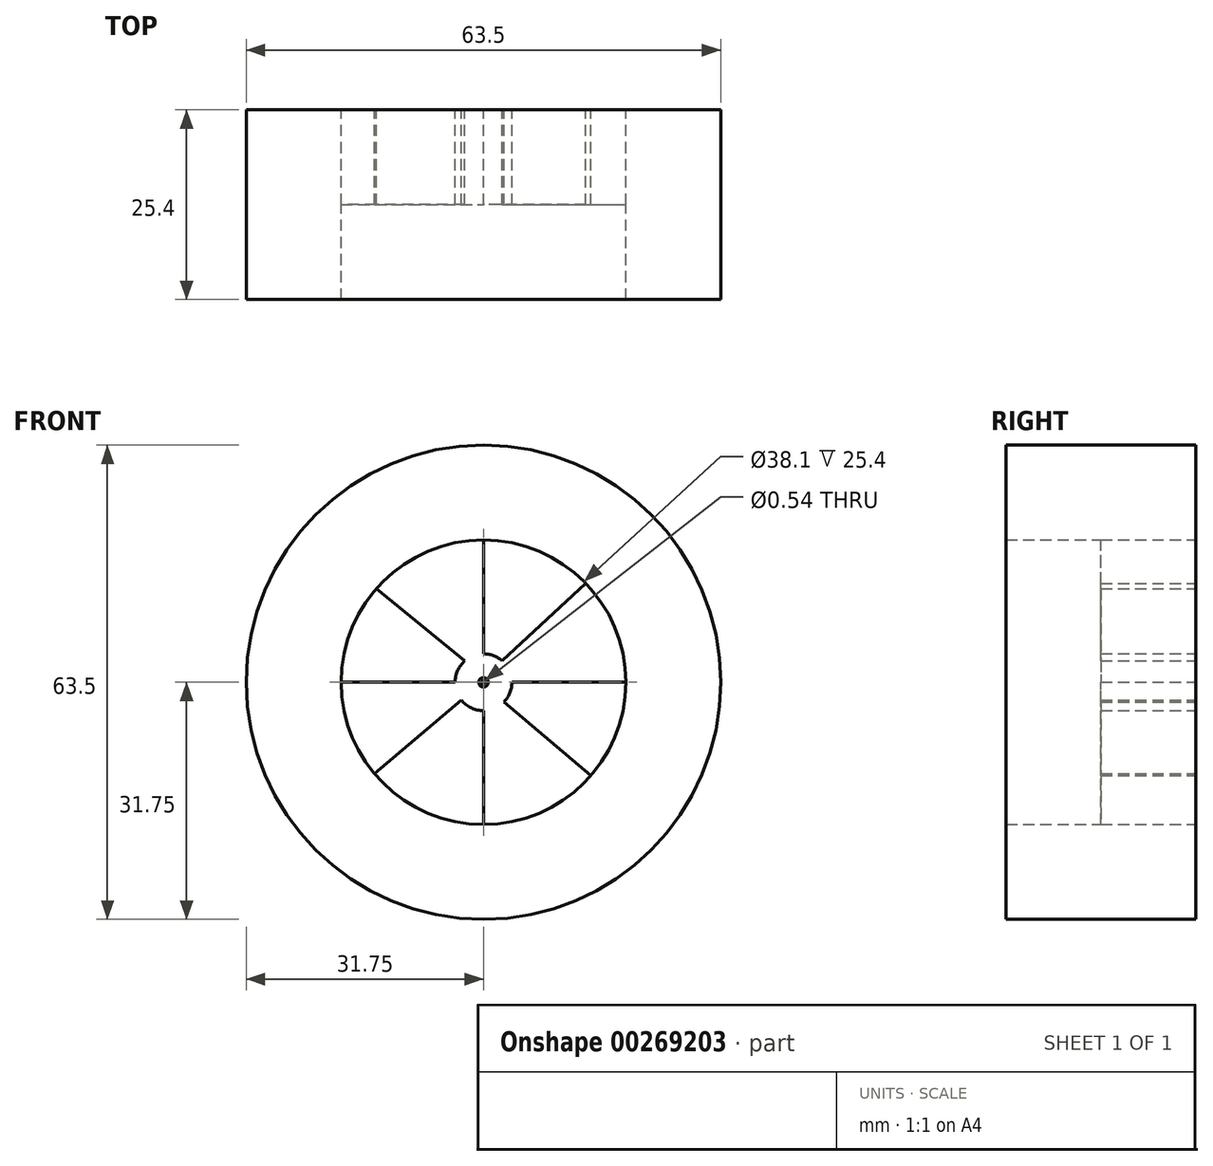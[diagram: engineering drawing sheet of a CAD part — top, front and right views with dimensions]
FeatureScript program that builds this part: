
annotation { "Feature Type Name" : "Feature", "Feature Type Description" : "" }
export const myFeature = defineFeature(function(context is Context, id is Id, definition is map)
    precondition{}
    {
        {
            var Q0;
            Q0=qCreatedBy(makeId("Front.planeOp"),FACE);
            var sketch = newSketch(context, id + "F0", { "sketchPlane" : qUnion([Q0])});
            skCircle(sketch, "E0", {"center": v(0, 0) * mm, "radius": 0.64 * mm});
            skCircle(sketch, "E1", {"center": v(0, 0) * mm, "radius": 0.27 * mm});
            skLineSegment(sketch, "E2", {"start": v(-0.27, 0) * mm, "end": v(0, 0) * mm});
            skLineSegment(sketch, "E3", {"start": v(0, 0.27) * mm, "end": v(0, 0) * mm});
            skLineSegment(sketch, "E4", {"start": v(0.27, 0) * mm, "end": v(0, 0) * mm});
            skLineSegment(sketch, "E5", {"start": v(0, -0.27) * mm, "end": v(0, 0) * mm});
            skCircle(sketch, "E6", {"center": v(0, 0) * mm, "radius": 0.04 * mm});
            skSolve(sketch);
        }
        {
            var Q0;
            Q0 = qSketchRegion(id + "F0", true);
            var Q1;
            Q1=makeQuery(id+"F0.imprint","IMPRINT",FACE,{"disambiguationData":[TD([[makeQuery(id+"F0.imprint","IMPRINT",EDGE,{"derivedFrom":sQuery(id+"F0.wireOp",EDGE,"E0")}),1.0]])]});
            extrude(context, id + "F1", {"entities" : qUnion([Q0, Q1]), "depth" : 0.08 * mm});
        }
        {
            var Q0;
            Q0=qCreatedBy(makeId("Front.planeOp"),FACE);
            var sketch = newSketch(context, id + "F2", { "sketchPlane" : qUnion([Q0])});
            skCircle(sketch, "E7", {"center": v(0, 0) * mm, "radius": 31.75 * mm});
            skCircle(sketch, "E8", {"center": v(0, 0) * mm, "radius": 19.05 * mm});
            skCircle(sketch, "E9", {"center": v(0, 0) * mm, "radius": 3.81 * mm});
            skLineSegment(sketch, "E10", {"start": v(0, 3.81) * mm, "end": v(0, 19.05) * mm});
            skLineSegment(sketch, "E11", {"start": v(3.81, 0) * mm, "end": v(19.05, 0) * mm});
            skLineSegment(sketch, "E12", {"start": v(0, -19.05) * mm, "end": v(0, -3.81) * mm});
            skLineSegment(sketch, "E13", {"start": v(-19.05, 0) * mm, "end": v(-3.81, 0) * mm});
            skLineSegment(sketch, "E14", {"start": v(2.77, -2.62) * mm, "end": v(14.37, -12.5) * mm});
            skLineSegment(sketch, "E15", {"start": v(-14.6, -12.23) * mm, "end": v(-2.98, -2.37) * mm});
            skLineSegment(sketch, "E16", {"start": v(-2.5, 2.87) * mm, "end": v(-14.36, 12.52) * mm});
            skLineSegment(sketch, "E17", {"start": v(2.47, 2.9) * mm, "end": v(13.68, 13.25) * mm});
            skSolve(sketch);
        }
        {
            var Q0;
            {var subQ0=sQuery(id+"F2.wireOp",EDGE,"E11");Q0=makeQuery(id+"F2.imprint","IMPRINT",FACE,{"disambiguationData":[TD([[makeQuery(id+"F2.imprint","IMPRINT",EDGE,{"derivedFrom":subQ0}),-1.0]])]});}
            var Q1;
            {var subQ0=sQuery(id+"F2.wireOp",EDGE,"E10");Q1=makeQuery(id+"F2.imprint","IMPRINT",FACE,{"disambiguationData":[TD([[makeQuery(id+"F2.imprint","IMPRINT",EDGE,{"derivedFrom":subQ0}),-1.0]])]});}
            var Q2;
            {var subQ0=sQuery(id+"F2.wireOp",EDGE,"E13");Q2=makeQuery(id+"F2.imprint","IMPRINT",FACE,{"disambiguationData":[TD([[makeQuery(id+"F2.imprint","IMPRINT",EDGE,{"derivedFrom":subQ0}),1.0]])]});}
            var Q3;
            {var subQ0=sQuery(id+"F2.wireOp",EDGE,"E12");Q3=makeQuery(id+"F2.imprint","IMPRINT",FACE,{"disambiguationData":[TD([[makeQuery(id+"F2.imprint","IMPRINT",EDGE,{"derivedFrom":subQ0}),1.0]])]});}
            extrude(context, id + "F3", {"entities" : qUnion([Q0, Q1, Q2, Q3]), "operationType" : NewBodyOperationType.ADD, "depth" : 12.7 * mm});
        }
        {
            var Q0;
            Q0 = qSketchRegion(id + "F2", true);
            extrude(context, id + "F4", {"entities" : qUnion([Q0]), "depth" : 25.4 * mm});
        }
        {
            var Q0;
            Q0 = qSketchRegion(id + "F2", true);
            extrude(context, id + "F5", {"entities" : qUnion([Q0]), "operationType" : NewBodyOperationType.ADD, "depth" : 25.4 * mm});
        }
        {
            var Q0;
            Q0 = qSketchRegion(id + "F2", true);
            extrude(context, id + "F6", {"entities" : qUnion([Q0]), "operationType" : NewBodyOperationType.ADD, "depth" : 25.4 * mm});
        }
    });
